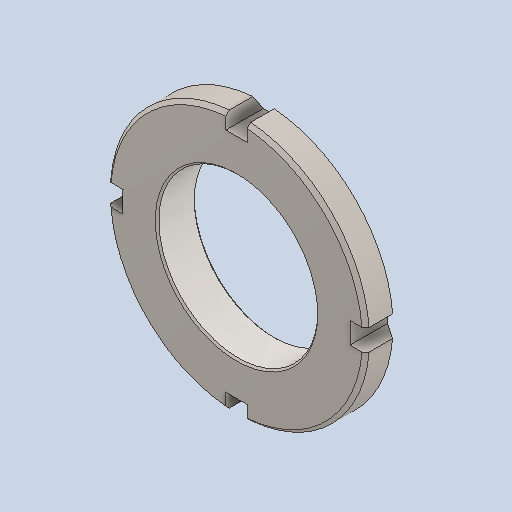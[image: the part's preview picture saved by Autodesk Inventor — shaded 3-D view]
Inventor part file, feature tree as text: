
AUTODESK INVENTOR PART (.ipt)
format: ipt  version: 2024.1 (Build 281209000, 209)  size: 139,776 bytes
history: native  units: in
note: dims shown in document units (in); Inventor stores cm internally (conversion verified against a paired STEP export)
features: chamfer x1
ambient origin geometry x8: Origin, YZ Plane, XZ Plane, XY Plane, X Axis, Y Axis, Z Axis, Center Point
bodies: Solid1 (feature_tree)
feature tree (1):
  chamfer  "Chamfer1"  [1 undecoded]
note: 1 required parameter value undecoded (feature->parameter linkage not recoverable at this tier; creation-order binding heuristic only, values carry confidence <= 0.55)
